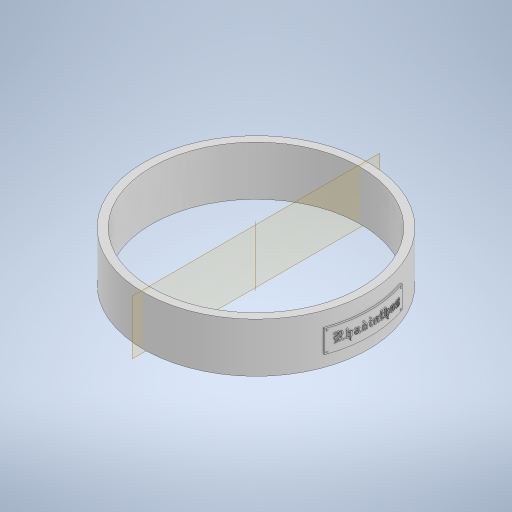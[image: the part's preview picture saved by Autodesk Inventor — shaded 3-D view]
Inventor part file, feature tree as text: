
AUTODESK INVENTOR PART (.ipt)
format: ipt  version: 2023 (Build 270158000, 158)  size: 4,828,672 bytes
history: native  units: in
note: dims shown in document units (in); Inventor stores cm internally (conversion verified against a paired STEP export)
features: emboss x3, pattern_circular x3, other x2, extrude x1, plane x1, fillet x1, sketch x1
ambient origin geometry x8: Origin, YZ Plane, XZ Plane, XY Plane, X Axis, Y Axis, Z Axis, Center Point
bodies: Solid1 (feature_tree)
feature tree (12):
  extrude  "Extrusion1"  Depth=0.3937in
  plane  "Work Plane1"
  other  "Text"
  emboss  "Emboss4"
  emboss  "Emboss5"
  emboss  "Emboss6"
  fillet  "Rivots"  Radius=0.8661in
  pattern_circular  "Circular Pattern1"  Count=6  [1 undecoded]
  pattern_circular  "Circular Pattern2"  [2 undecoded]
  pattern_circular  "Circular Pattern3"  [2 undecoded]
  sketch  "Sketch1"  dims[d0=3.937in d1=3.6614in d2=0.8661in d3=0.0in d4=2.3622in d6=0.4546in d10=0.0in d11=0.3937in d12=1.378in d19=0.0in d20=0.0in d21=0.0295in d22=0.0in d23=0.0197in d24=0.0in d25=0.0295in d26=0.0295in d27=0.0295in d28=0.0157in d29=0.0in d30=0.0138in d31=0.7874in d32=360.0deg d34=0.7874in d35=360.0deg d37=0.7874in d38=360.0deg d33=0.0in]
  other  "NamePlate"
note: 5 required parameter values undecoded (feature->parameter linkage not recoverable at this tier; creation-order binding heuristic only, values carry confidence <= 0.55)
